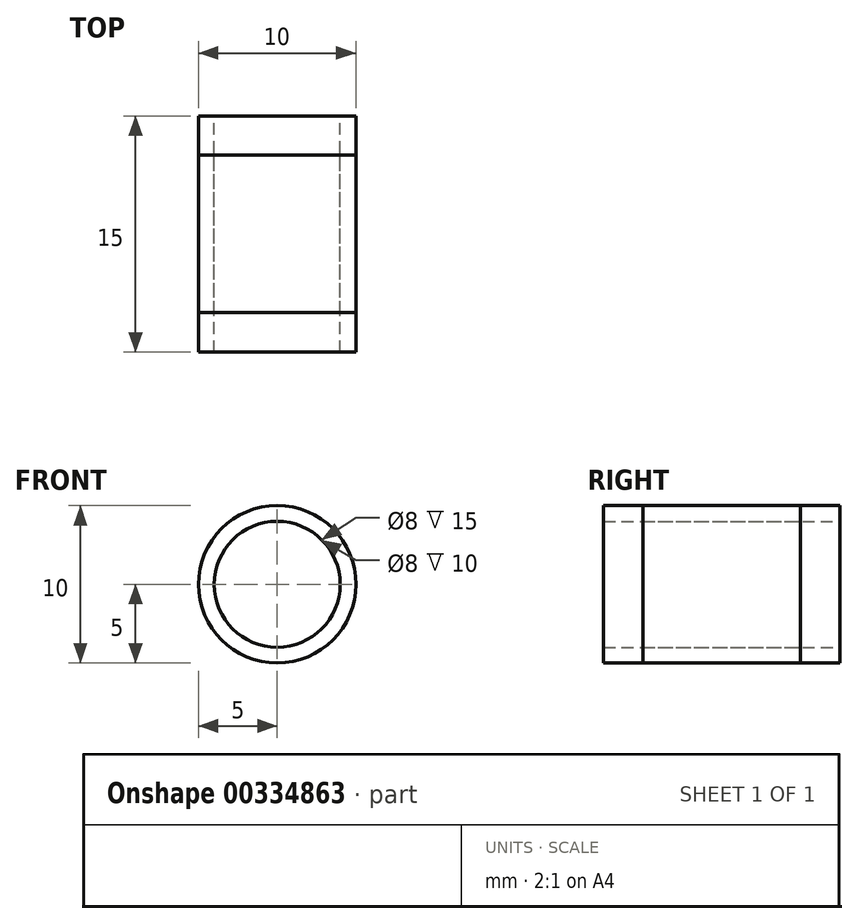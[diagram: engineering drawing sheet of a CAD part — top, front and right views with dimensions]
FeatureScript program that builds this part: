
annotation { "Feature Type Name" : "Feature", "Feature Type Description" : "" }
export const myFeature = defineFeature(function(context is Context, id is Id, definition is map)
    precondition{}
    {
        {
            var Q0;
            Q0=qCreatedBy(makeId("Front.planeOp"),FACE);
            var sketch = newSketch(context, id + "F0", { "sketchPlane" : qUnion([Q0])});
            skCircle(sketch, "E0", {"center": v(0, 0) * mm, "radius": 5 * mm});
            skCircle(sketch, "E1", {"center": v(0, 0) * mm, "radius": 4 * mm});
            skSolve(sketch);
        }
        {
            var Q0;
            Q0 = qSketchRegion(id + "F0", true);
            extrude(context, id + "F1", {"entities" : qUnion([Q0]), "endBound" : BoundingType.SYMMETRIC, "depth" : 10 * mm});
        }
        {
            var Q0;
            Q0 = qSketchRegion(id + "F0", true);
            extrude(context, id + "F2", {"entities" : qUnion([Q0]), "endBound" : BoundingType.SYMMETRIC, "depth" : 15 * mm});
        }
    });
